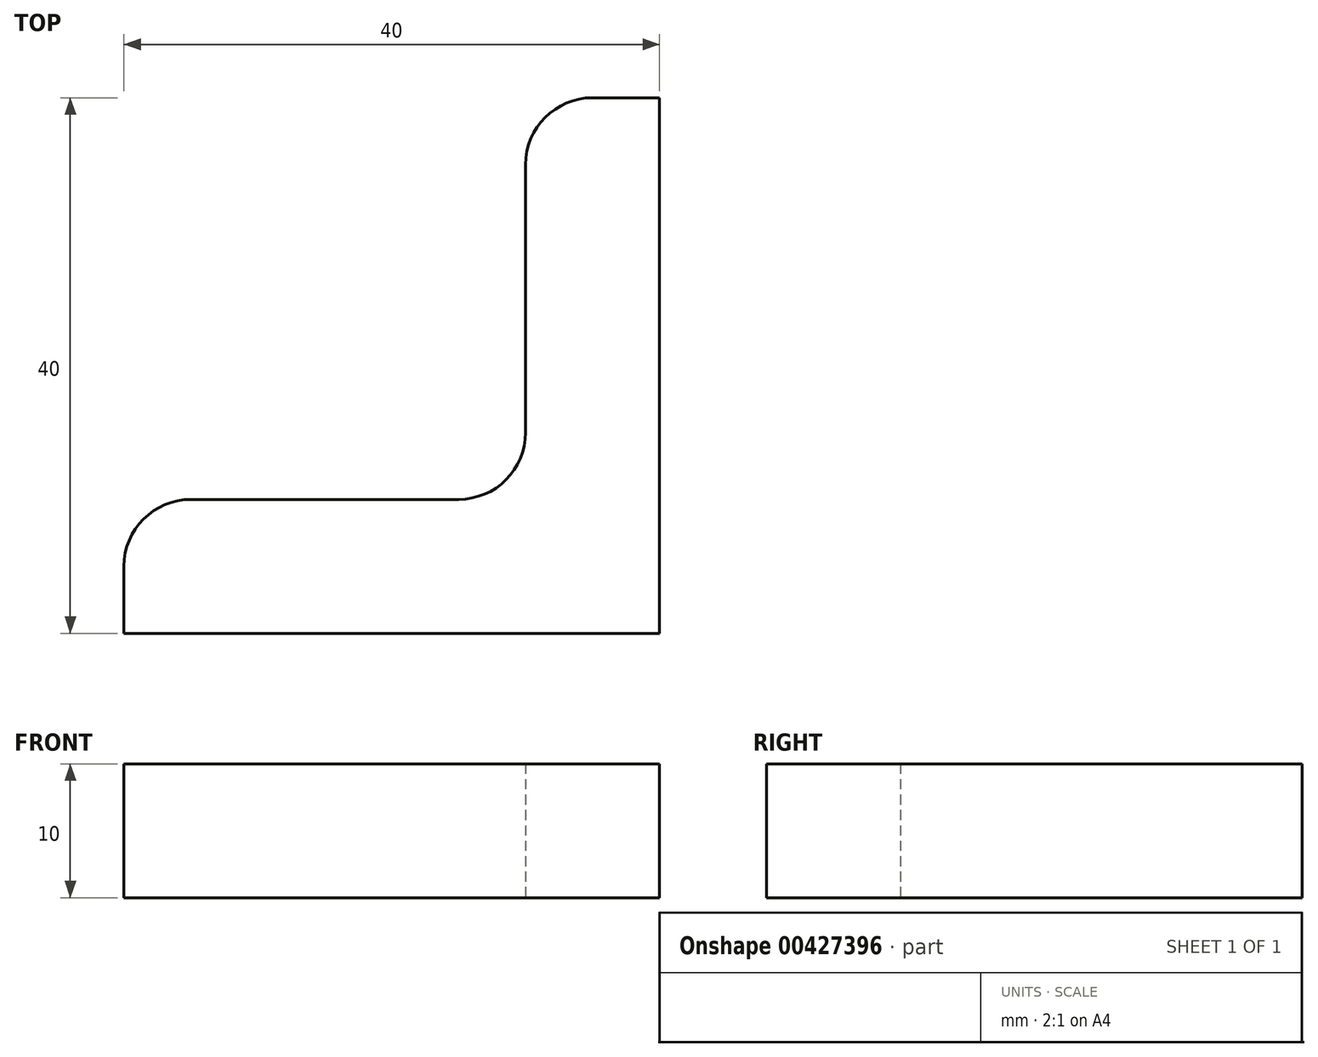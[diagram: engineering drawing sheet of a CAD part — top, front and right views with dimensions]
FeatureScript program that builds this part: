
annotation { "Feature Type Name" : "Feature", "Feature Type Description" : "" }
export const myFeature = defineFeature(function(context is Context, id is Id, definition is map)
    precondition{}
    {
        {
            var Q0;
            Q0=qCreatedBy(makeId("Top.planeOp"),FACE);
            var sketch = newSketch(context, id + "F0", { "sketchPlane" : qUnion([Q0])});
            skLineSegment(sketch, "E0.bottom", {"start": v(-22.27, -14.03) * mm, "end": v(17.73, -14.03) * mm});
            skLineSegment(sketch, "E0.top", {"start": v(-22.27, -4.03) * mm, "end": v(17.73, -4.03) * mm});
            skLineSegment(sketch, "E0.left", {"start": v(-22.27, -14.03) * mm, "end": v(-22.27, -4.03) * mm});
            skLineSegment(sketch, "E0.right", {"start": v(17.73, -14.03) * mm, "end": v(17.73, -4.03) * mm});
            skLineSegment(sketch, "E1.bottom", {"start": v(17.73, -14.03) * mm, "end": v(7.73, -14.03) * mm});
            skLineSegment(sketch, "E1.top", {"start": v(17.73, 25.97) * mm, "end": v(7.73, 25.97) * mm});
            skLineSegment(sketch, "E1.left", {"start": v(17.73, -14.03) * mm, "end": v(17.73, 25.97) * mm});
            skLineSegment(sketch, "E1.right", {"start": v(7.73, -14.03) * mm, "end": v(7.73, 25.97) * mm});
            skSolve(sketch);
        }
        {
            var Q0;
            {var subQ5=sQuery(id+"F0.wireOp",EDGE,"E1.top");Q0=makeQuery(id+"F0.imprint","IMPRINT",FACE,{"disambiguationData":[TD([[makeQuery(id+"F0.imprint","IMPRINT",EDGE,{"derivedFrom":subQ5}),1.0]])]});}
            var Q1;
            {var subQ5=sQuery(id+"F0.wireOp",EDGE,"E1.bottom");Q1=makeQuery(id+"F0.imprint","IMPRINT",FACE,{"disambiguationData":[TD([[makeQuery(id+"F0.imprint","IMPRINT",EDGE,{"derivedFrom":subQ5}),-1.0]])]});}
            var Q2;
            {var subQ0=sQuery(id+"F0.wireOp",EDGE,"E0.bottom");Q2=makeQuery(id+"F0.imprint","IMPRINT",FACE,{"disambiguationData":[TD([[makeQuery(id+"F0.imprint","IMPRINT",EDGE,{"derivedFrom":subQ0}),1.0]])]});}
            extrude(context, id + "F1", {"entities" : qUnion([Q0, Q1, Q2]), "depth" : 10 * mm});
        }
        {
            var Q0;
            Q0=makeQuery(id+"F1.opExtrude","SWEPT_EDGE",EDGE,{"disambiguationData":[OSD([sQuery(id+"F0.wireOp",EDGE,"E0.top"),sQuery(id+"F0.wireOp",EDGE,"E1.right")])]});
            var Q1;
            Q1=makeQuery(id+"F1.opExtrude","SWEPT_EDGE",EDGE,{"disambiguationData":[OSD([sQuery(id+"F0.wireOp",EDGE,"E1.top"),sQuery(id+"F0.wireOp",EDGE,"E1.right")])]});
            var Q2;
            Q2=makeQuery(id+"F1.opExtrude","SWEPT_EDGE",EDGE,{"disambiguationData":[OSD([sQuery(id+"F0.wireOp",EDGE,"E0.top"),sQuery(id+"F0.wireOp",EDGE,"E0.left")])]});
            fillet(context, id + "F2", {"entities" : qUnion([Q0, Q1, Q2]), "radius" : 5 * mm, "tangentPropagation" : true, "allowEdgeOverflow" : false});
        }
    });
